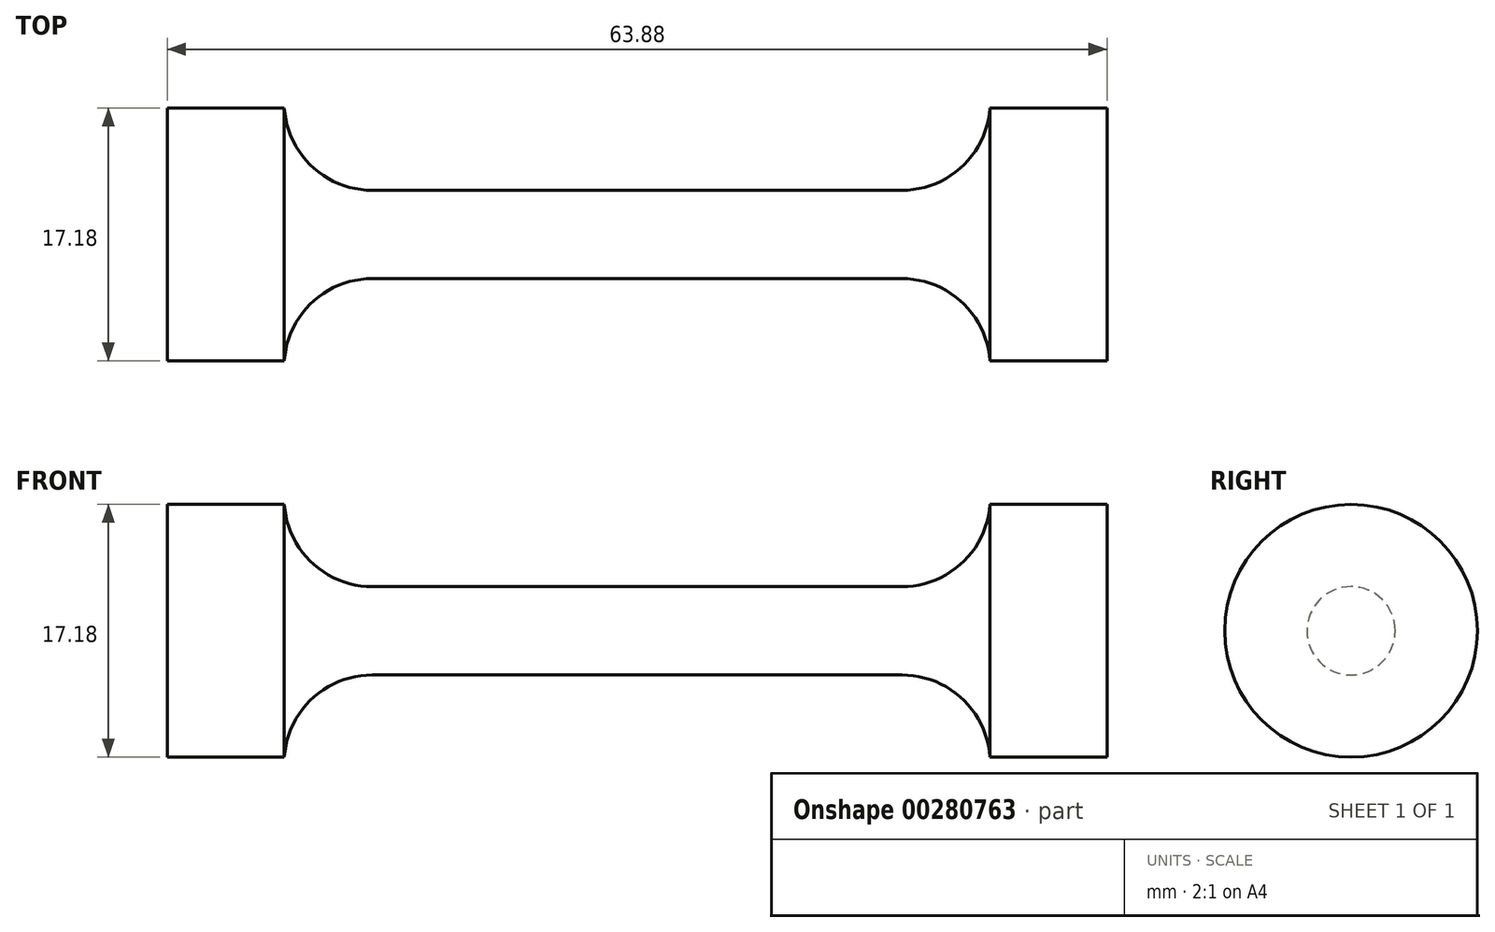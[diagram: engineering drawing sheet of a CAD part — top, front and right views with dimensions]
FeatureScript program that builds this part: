
annotation { "Feature Type Name" : "Feature", "Feature Type Description" : "" }
export const myFeature = defineFeature(function(context is Context, id is Id, definition is map)
    precondition{}
    {
        {
            var Q0;
            Q0=qCreatedBy(makeId("Front.planeOp"),FACE);
            var sketch = newSketch(context, id + "F0", { "sketchPlane" : qUnion([Q0])});
            skLineSegment(sketch, "E0", {"start": v(0, 3) * mm, "end": v(18, 3) * mm});
            skArc(sketch, "E1", {"start": v(18, 3) * mm, "mid": v(22.1, 4.61) * mm, "end": v(23.99, 8.59) * mm});
            skLineSegment(sketch, "E2", {"start": v(23.99, 8.59) * mm, "end": v(31.94, 8.59) * mm});
            skLineSegment(sketch, "E3", {"start": v(31.94, 8.59) * mm, "end": v(31.94, 0) * mm});
            skLineSegment(sketch, "E4.MirrorCS", {"start": v(-23.99, 8.59) * mm, "end": v(-31.94, 8.59) * mm});
            skLineSegment(sketch, "E5.MirrorCS", {"start": v(-31.94, 8.59) * mm, "end": v(-31.94, 0) * mm});
            skLineSegment(sketch, "E6.MirrorCS", {"start": v(0, 3) * mm, "end": v(-18, 3) * mm});
            skArc(sketch, "E7.MirrorCS", {"start": v(-18, 3) * mm, "mid": v(-22.1, 4.61) * mm, "end": v(-23.99, 8.59) * mm});
            skLineSegment(sketch, "E8", {"start": v(-31.94, 0) * mm, "end": v(31.94, 0) * mm});
            skSolve(sketch);
        }
        {
            var Q0;
            Q0 = qSketchRegion(id + "F0", true);
            var Q1;
            Q1=sQuery(id+"F0.wireOp",EDGE,"E8");
            revolve(context, id + "F1", {"entities" : qUnion([Q0]), "axis" : qUnion([Q1]), "revolveType" : RevolveType.FULL});
        }
    });
